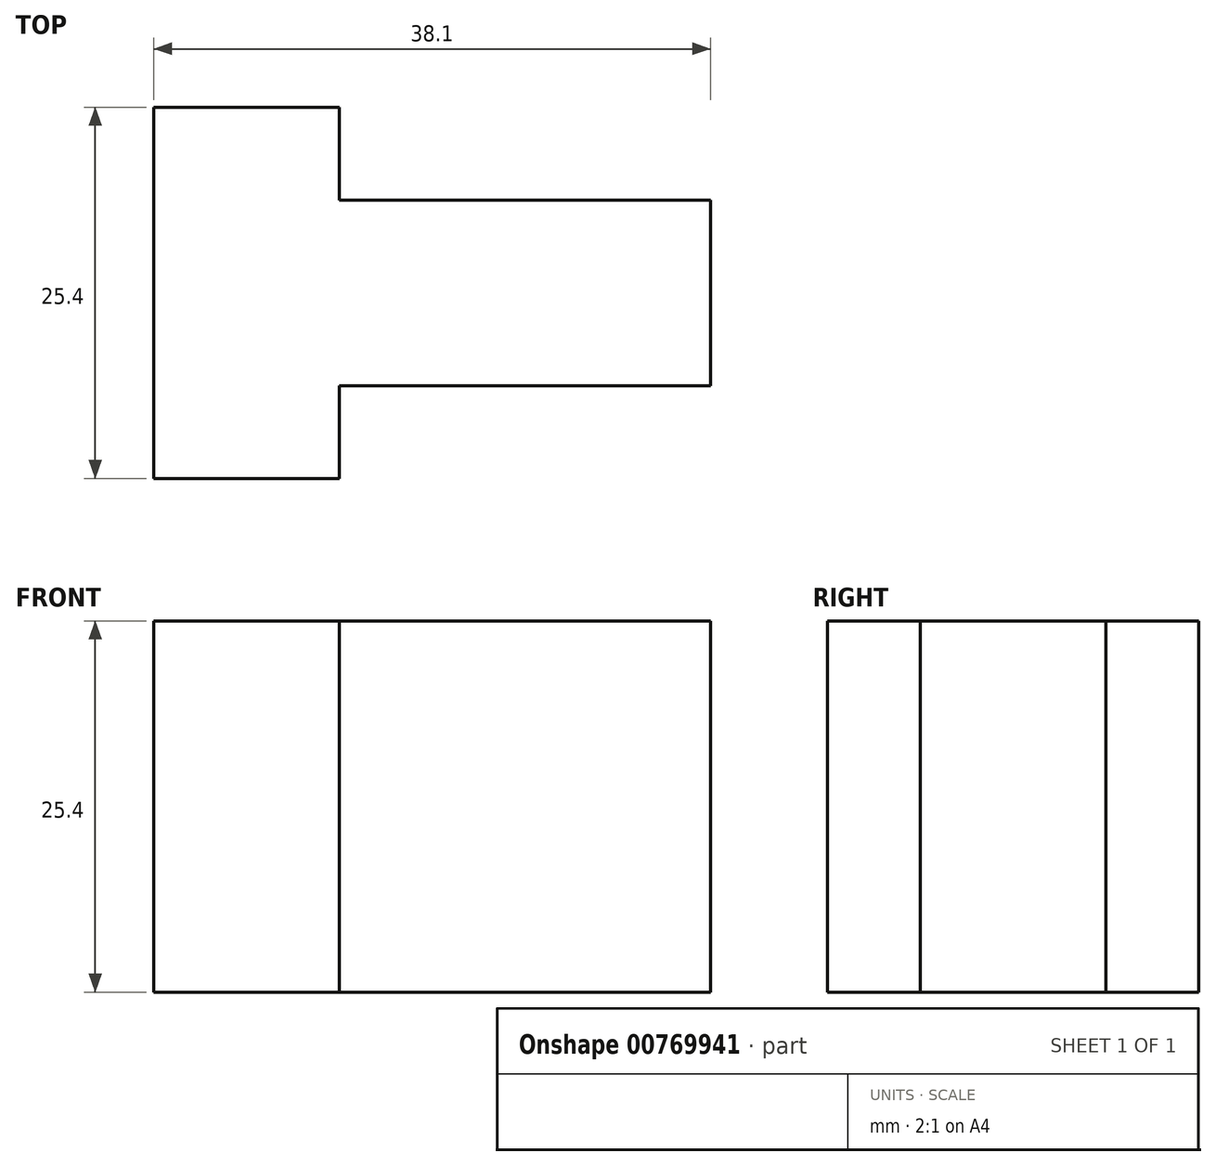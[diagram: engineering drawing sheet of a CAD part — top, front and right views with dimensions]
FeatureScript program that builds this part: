
annotation { "Feature Type Name" : "Feature", "Feature Type Description" : "" }
export const myFeature = defineFeature(function(context is Context, id is Id, definition is map)
    precondition{}
    {
        {
            var Q0;
            Q0=qCreatedBy(makeId("Top.planeOp"),FACE);
            var sketch = newSketch(context, id + "F0", { "sketchPlane" : qUnion([Q0])});
            skLineSegment(sketch, "E0", {"start": v(0, 0) * mm, "end": v(12.7, 0) * mm});
            skLineSegment(sketch, "E1", {"start": v(12.7, 0) * mm, "end": v(12.7, 6.35) * mm});
            skLineSegment(sketch, "E2", {"start": v(12.7, 6.35) * mm, "end": v(38.1, 6.35) * mm});
            skLineSegment(sketch, "E3", {"start": v(38.1, 6.35) * mm, "end": v(38.1, 19.05) * mm});
            skLineSegment(sketch, "E4", {"start": v(38.1, 19.05) * mm, "end": v(12.7, 19.05) * mm});
            skLineSegment(sketch, "E5", {"start": v(12.7, 19.05) * mm, "end": v(12.7, 25.4) * mm});
            skLineSegment(sketch, "E6", {"start": v(12.7, 25.4) * mm, "end": v(0, 25.4) * mm});
            skLineSegment(sketch, "E7", {"start": v(0, 25.4) * mm, "end": v(0, 0) * mm});
            skSolve(sketch);
        }
        {
            var Q0;
            Q0 = qSketchRegion(id + "F0", true);
            extrude(context, id + "F1", {"entities" : qUnion([Q0]), "depth" : 25.4 * mm, "offsetDistance" : 25.4 * mm});
        }
    });
